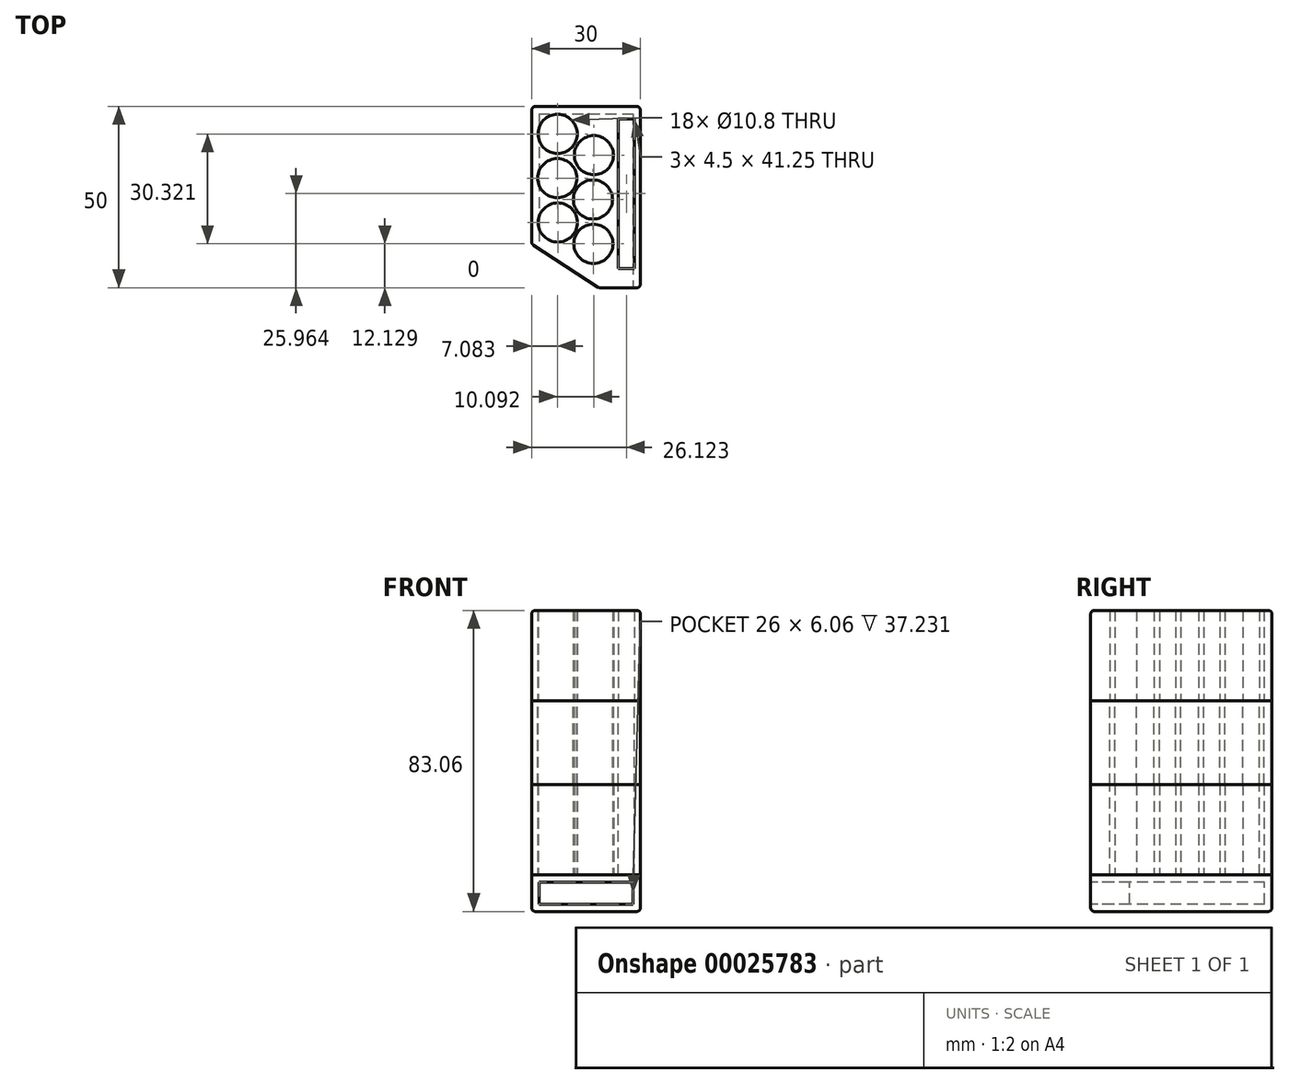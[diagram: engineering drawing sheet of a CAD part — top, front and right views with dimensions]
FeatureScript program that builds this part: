
annotation { "Feature Type Name" : "Feature", "Feature Type Description" : "" }
export const myFeature = defineFeature(function(context is Context, id is Id, definition is map)
    precondition{}
    {
        {
            var Q0;
            Q0=qCreatedBy(makeId("Top.planeOp"),FACE);
            var sketch = newSketch(context, id + "F0", { "sketchPlane" : qUnion([Q0])});
            skLineSegment(sketch, "E0.bottom", {"start": v(-10.19, 25.73) * mm, "end": v(19.81, 25.73) * mm});
            skLineSegment(sketch, "E0.top", {"start": v(8.4, -24.27) * mm, "end": v(19.81, -24.27) * mm});
            skLineSegment(sketch, "E0.left", {"start": v(-10.19, 25.73) * mm, "end": v(-10.19, -12.2) * mm});
            skLineSegment(sketch, "E0.right", {"start": v(19.81, 25.73) * mm, "end": v(19.81, -24.27) * mm});
            skCircle(sketch, "E1", {"center": v(-3.04, 18.18) * mm, "radius": 5.4 * mm});
            skCircle(sketch, "E2", {"center": v(6.98, 12.3) * mm, "radius": 5.4 * mm});
            skCircle(sketch, "E3", {"center": v(-3.1, 5.96) * mm, "radius": 5.4 * mm});
            skCircle(sketch, "E4", {"center": v(6.72, 0.09) * mm, "radius": 5.4 * mm});
            skCircle(sketch, "E5", {"center": v(-2.98, -6.26) * mm, "radius": 5.4 * mm});
            skCircle(sketch, "E6", {"center": v(6.85, -12.14) * mm, "radius": 5.4 * mm});
            skLineSegment(sketch, "E7.bottom", {"start": v(13.68, -18.93) * mm, "end": v(18.18, -18.93) * mm});
            skLineSegment(sketch, "E7.top", {"start": v(13.68, 22.32) * mm, "end": v(18.18, 22.32) * mm});
            skLineSegment(sketch, "E7.left", {"start": v(13.68, -18.93) * mm, "end": v(13.68, 22.32) * mm});
            skLineSegment(sketch, "E7.right", {"start": v(18.18, -18.93) * mm, "end": v(18.18, 22.32) * mm});
            skLineSegment(sketch, "E8", {"start": v(-10.19, -12.2) * mm, "end": v(8.4, -24.27) * mm});
            skSolve(sketch);
        }
        {
            var Q0;
            Q0=makeQuery(id+"F0.imprint","IMPRINT",FACE,{"disambiguationData":[TD([[makeQuery(id+"F0.imprint","IMPRINT",EDGE,{"derivedFrom":sQuery(id+"F0.wireOp",EDGE,"E0.bottom")}),-1.0]])]});
            extrude(context, id + "F1", {"entities" : qUnion([Q0]), "depth" : 25 * mm});
        }
        {
            var Q0;
            Q0=makeQuery(id+"F0.imprint","IMPRINT",FACE,{"disambiguationData":[TD([[makeQuery(id+"F0.imprint","IMPRINT",EDGE,{"derivedFrom":sQuery(id+"F0.wireOp",EDGE,"E7.bottom")}),1.0]])]});
            var Q1;
            Q1=makeQuery(id+"F0.imprint","IMPRINT",FACE,{"disambiguationData":[TD([[makeQuery(id+"F0.imprint","IMPRINT",EDGE,{"derivedFrom":sQuery(id+"F0.wireOp",EDGE,"E6")}),1.0]])]});
            var Q2;
            Q2=makeQuery(id+"F0.imprint","IMPRINT",FACE,{"disambiguationData":[TD([[makeQuery(id+"F0.imprint","IMPRINT",EDGE,{"derivedFrom":sQuery(id+"F0.wireOp",EDGE,"E5")}),1.0]])]});
            var Q3;
            Q3=makeQuery(id+"F0.imprint","IMPRINT",FACE,{"disambiguationData":[TD([[makeQuery(id+"F0.imprint","IMPRINT",EDGE,{"derivedFrom":sQuery(id+"F0.wireOp",EDGE,"E3")}),1.0]])]});
            var Q4;
            Q4=makeQuery(id+"F0.imprint","IMPRINT",FACE,{"disambiguationData":[TD([[makeQuery(id+"F0.imprint","IMPRINT",EDGE,{"derivedFrom":sQuery(id+"F0.wireOp",EDGE,"E4")}),1.0]])]});
            var Q5;
            Q5=makeQuery(id+"F0.imprint","IMPRINT",FACE,{"disambiguationData":[TD([[makeQuery(id+"F0.imprint","IMPRINT",EDGE,{"derivedFrom":sQuery(id+"F0.wireOp",EDGE,"E2")}),1.0]])]});
            var Q6;
            Q6=makeQuery(id+"F0.imprint","IMPRINT",FACE,{"disambiguationData":[TD([[makeQuery(id+"F0.imprint","IMPRINT",EDGE,{"derivedFrom":sQuery(id+"F0.wireOp",EDGE,"E1")}),1.0]])]});
            var Q7;
            Q7=makeQuery(id+"F0.imprint","IMPRINT",FACE,{"disambiguationData":[TD([[makeQuery(id+"F0.imprint","IMPRINT",EDGE,{"derivedFrom":sQuery(id+"F0.wireOp",EDGE,"E0.bottom")}),-1.0]])]});
            extrude(context, id + "F2", {"entities" : qUnion([Q0, Q1, Q2, Q3, Q4, Q5, Q6, Q7]), "oppositeDirection" : true, "depth" : 10.06 * mm});
        }
        {
            var Q0;
            Q0=makeQuery(id+"F1.opExtrude","CAP_FACE",FACE,{"disambiguationData":[OSD([sQuery(id+"F0.wireOp",EDGE,"E0.bottom"),sQuery(id+"F0.wireOp",EDGE,"E0.top"),sQuery(id+"F0.wireOp",EDGE,"E0.left"),sQuery(id+"F0.wireOp",EDGE,"E0.right"),sQuery(id+"F0.wireOp",EDGE,"E1"),sQuery(id+"F0.wireOp",EDGE,"E2"),sQuery(id+"F0.wireOp",EDGE,"E3"),sQuery(id+"F0.wireOp",EDGE,"E4"),sQuery(id+"F0.wireOp",EDGE,"E5"),sQuery(id+"F0.wireOp",EDGE,"E6"),sQuery(id+"F0.wireOp",EDGE,"E7.bottom"),sQuery(id+"F0.wireOp",EDGE,"E7.top"),sQuery(id+"F0.wireOp",EDGE,"E7.left"),sQuery(id+"F0.wireOp",EDGE,"E7.right"),sQuery(id+"F0.wireOp",EDGE,"E8")])],"isStart":false});
            var sketch = newSketch(context, id + "F3", { "sketchPlane" : qUnion([Q0])});
            skLineSegment(sketch, "E9.bottom", {"start": v(13.68, -18.93) * mm, "end": v(18.18, -18.93) * mm});
            skLineSegment(sketch, "E9.top", {"start": v(13.68, 22.32) * mm, "end": v(18.18, 22.32) * mm});
            skLineSegment(sketch, "E9.left", {"start": v(13.68, -18.93) * mm, "end": v(13.68, 22.32) * mm});
            skLineSegment(sketch, "E9.right", {"start": v(18.18, -18.93) * mm, "end": v(18.18, 22.32) * mm});
            skSolve(sketch);
        }
        {
            var Q0;
            Q0 = qSketchRegion(id + "F3", true);
            extrude(context, id + "F4", {"entities" : qUnion([Q0]), "oppositeDirection" : true, "depth" : 25 * mm});
        }
        {
            var Q0;
            Q0=makeQuery(id+"F1.opExtrude","SWEPT_BODY",BODY,{"disambiguationData":[OSD([sQuery(id+"F0.wireOp",EDGE,"E0.bottom"),sQuery(id+"F0.wireOp",EDGE,"E0.top"),sQuery(id+"F0.wireOp",EDGE,"E0.left"),sQuery(id+"F0.wireOp",EDGE,"E0.right"),sQuery(id+"F0.wireOp",EDGE,"E1"),sQuery(id+"F0.wireOp",EDGE,"E2"),sQuery(id+"F0.wireOp",EDGE,"E3"),sQuery(id+"F0.wireOp",EDGE,"E4"),sQuery(id+"F0.wireOp",EDGE,"E5"),sQuery(id+"F0.wireOp",EDGE,"E6"),sQuery(id+"F0.wireOp",EDGE,"E7.bottom"),sQuery(id+"F0.wireOp",EDGE,"E7.top"),sQuery(id+"F0.wireOp",EDGE,"E7.left"),sQuery(id+"F0.wireOp",EDGE,"E7.right"),sQuery(id+"F0.wireOp",EDGE,"E8")])]});
            var Q1;
            Q1=makeQuery(id+"F1.opExtrude","SWEPT_EDGE",EDGE,{"disambiguationData":[OSD([sQuery(id+"F0.wireOp",EDGE,"E0.top"),sQuery(id+"F0.wireOp",EDGE,"E0.right")])]});
            var Q2;
            Q2=makeQuery(id+"F1.opExtrude","CAP_VERTEX",VERTEX,{"disambiguationData":[OSD([sQuery(id+"F0.wireOp",EDGE,"E0.top"),sQuery(id+"F0.wireOp",EDGE,"E0.right")])],"isStart":false});
            transform(context, id + "F5", {"entities" : qUnion([Q0]), "transformType" : TransformType.TRANSLATION_DISTANCE, "transformDirection" : qUnion([Q1]), "distance" : 48 * mm, "oppositeDirection" : true, "makeCopy" : true});
        }
        {
            var Q0;
            Q0=makeQuery(id+"F2.opExtrude","SWEPT_FACE",FACE,{"disambiguationData":[OSD([sQuery(id+"F0.wireOp",EDGE,"E0.top")])]});
            var Q1;
            Q1=makeQuery(id+"F2.opExtrude","SWEPT_FACE",FACE,{"disambiguationData":[OSD([sQuery(id+"F0.wireOp",EDGE,"E8")])]});
            shell(context, id + "F6", {"entities" : qUnion([Q0, Q1]), "thickness" : 2 * mm});
        }
        {
            var Q0;
            Q0=makeQuery(id+"F5.opPattern","COPY",EDGE,{"derivedFrom":makeQuery(id+"F1.opExtrude","CAP_EDGE",EDGE,{"disambiguationData":[OSD([sQuery(id+"F0.wireOp",EDGE,"E0.left")])],"isStart":false}),"instanceName":"1"});
            var Q1;
            Q1=makeQuery(id+"F5.opPattern","COPY",EDGE,{"derivedFrom":makeQuery(id+"F1.opExtrude","CAP_EDGE",EDGE,{"disambiguationData":[OSD([sQuery(id+"F0.wireOp",EDGE,"E8")])],"isStart":false}),"instanceName":"1"});
            var Q2;
            Q2=makeQuery(id+"F5.opPattern","COPY",EDGE,{"derivedFrom":makeQuery(id+"F1.opExtrude","CAP_EDGE",EDGE,{"disambiguationData":[OSD([sQuery(id+"F0.wireOp",EDGE,"E0.top")])],"isStart":false}),"instanceName":"1"});
            var Q3;
            Q3=makeQuery(id+"F5.opPattern","COPY",EDGE,{"derivedFrom":makeQuery(id+"F1.opExtrude","CAP_EDGE",EDGE,{"disambiguationData":[OSD([sQuery(id+"F0.wireOp",EDGE,"E0.bottom")])],"isStart":false}),"instanceName":"1"});
            var Q4;
            Q4=makeQuery(id+"F5.opPattern","COPY",EDGE,{"derivedFrom":makeQuery(id+"F1.opExtrude","CAP_EDGE",EDGE,{"disambiguationData":[OSD([sQuery(id+"F0.wireOp",EDGE,"E0.right")])],"isStart":false}),"instanceName":"1"});
            fillet(context, id + "F7", {"entities" : qUnion([Q0, Q1, Q2, Q3, Q4]), "radius" : 1 * mm, "tangentPropagation" : true, "allowEdgeOverflow" : false});
        }
        {
            var Q0;
            Q0=makeQuery(id+"F2.opExtrude","CAP_EDGE",EDGE,{"disambiguationData":[OSD([sQuery(id+"F0.wireOp",EDGE,"E0.left")])],"isStart":false});
            var Q1;
            Q1=makeQuery(id+"F2.opExtrude","CAP_EDGE",EDGE,{"disambiguationData":[OSD([sQuery(id+"F0.wireOp",EDGE,"E8")])],"isStart":false});
            var Q2;
            Q2=makeQuery(id+"F2.opExtrude","CAP_EDGE",EDGE,{"disambiguationData":[OSD([sQuery(id+"F0.wireOp",EDGE,"E0.top")])],"isStart":false});
            var Q3;
            Q3=makeQuery(id+"F2.opExtrude","CAP_EDGE",EDGE,{"disambiguationData":[OSD([sQuery(id+"F0.wireOp",EDGE,"E0.right")])],"isStart":false});
            var Q4;
            Q4=makeQuery(id+"F2.opExtrude","CAP_EDGE",EDGE,{"disambiguationData":[OSD([sQuery(id+"F0.wireOp",EDGE,"E0.bottom")])],"isStart":false});
            fillet(context, id + "F8", {"entities" : qUnion([Q0, Q1, Q2, Q3, Q4]), "radius" : 1 * mm, "tangentPropagation" : true, "allowEdgeOverflow" : false});
        }
        {
            var Q0;
            Q0=makeQuery(id+"F5.opPattern","COPY",FACE,{"derivedFrom":makeQuery(id+"F1.opExtrude","CAP_FACE",FACE,{"disambiguationData":[OSD([sQuery(id+"F0.wireOp",EDGE,"E0.bottom"),sQuery(id+"F0.wireOp",EDGE,"E0.top"),sQuery(id+"F0.wireOp",EDGE,"E0.left"),sQuery(id+"F0.wireOp",EDGE,"E0.right"),sQuery(id+"F0.wireOp",EDGE,"E1"),sQuery(id+"F0.wireOp",EDGE,"E2"),sQuery(id+"F0.wireOp",EDGE,"E3"),sQuery(id+"F0.wireOp",EDGE,"E4"),sQuery(id+"F0.wireOp",EDGE,"E5"),sQuery(id+"F0.wireOp",EDGE,"E6"),sQuery(id+"F0.wireOp",EDGE,"E7.bottom"),sQuery(id+"F0.wireOp",EDGE,"E7.top"),sQuery(id+"F0.wireOp",EDGE,"E7.left"),sQuery(id+"F0.wireOp",EDGE,"E7.right"),sQuery(id+"F0.wireOp",EDGE,"E8")])],"isStart":true}),"instanceName":"1"});
            extrude(context, id + "F9", {"entities" : qUnion([Q0]), "depth" : 23 * mm});
        }
        {
            var Q0;
            Q0=makeQuery(id+"F5.opPattern","COPY",EDGE,{"derivedFrom":makeQuery(id+"F1.opExtrude","SWEPT_EDGE",EDGE,{"disambiguationData":[OSD([sQuery(id+"F0.wireOp",EDGE,"E0.left"),sQuery(id+"F0.wireOp",EDGE,"E8")])]}),"instanceName":"1"});
            var Q1;
            Q1=makeQuery(id+"F9.opExtrude","SWEPT_EDGE",EDGE,{"disambiguationData":[OSD([sQuery(id+"F0.wireOp",EDGE,"E0.left"),sQuery(id+"F0.wireOp",EDGE,"E8")])]});
            var Q2;
            Q2=makeQuery(id+"F1.opExtrude","SWEPT_EDGE",EDGE,{"disambiguationData":[OSD([sQuery(id+"F0.wireOp",EDGE,"E0.left"),sQuery(id+"F0.wireOp",EDGE,"E8")])]});
            var Q3;
            Q3=makeQuery(id+"F5.opPattern","COPY",EDGE,{"derivedFrom":makeQuery(id+"F1.opExtrude","SWEPT_EDGE",EDGE,{"disambiguationData":[OSD([sQuery(id+"F0.wireOp",EDGE,"E0.top"),sQuery(id+"F0.wireOp",EDGE,"E8")])]}),"instanceName":"1"});
            var Q4;
            Q4=makeQuery(id+"F9.opExtrude","SWEPT_EDGE",EDGE,{"disambiguationData":[OSD([sQuery(id+"F0.wireOp",EDGE,"E0.top"),sQuery(id+"F0.wireOp",EDGE,"E8")])]});
            var Q5;
            Q5=makeQuery(id+"F1.opExtrude","SWEPT_EDGE",EDGE,{"disambiguationData":[OSD([sQuery(id+"F0.wireOp",EDGE,"E0.top"),sQuery(id+"F0.wireOp",EDGE,"E8")])]});
            var Q6;
            Q6=makeQuery(id+"F5.opPattern","COPY",EDGE,{"derivedFrom":makeQuery(id+"F1.opExtrude","SWEPT_EDGE",EDGE,{"disambiguationData":[OSD([sQuery(id+"F0.wireOp",EDGE,"E0.top"),sQuery(id+"F0.wireOp",EDGE,"E0.right")])]}),"instanceName":"1"});
            var Q7;
            Q7=makeQuery(id+"F9.opExtrude","SWEPT_EDGE",EDGE,{"disambiguationData":[OSD([sQuery(id+"F0.wireOp",EDGE,"E0.top"),sQuery(id+"F0.wireOp",EDGE,"E0.right")])]});
            var Q8;
            Q8=makeQuery(id+"F1.opExtrude","SWEPT_EDGE",EDGE,{"disambiguationData":[OSD([sQuery(id+"F0.wireOp",EDGE,"E0.top"),sQuery(id+"F0.wireOp",EDGE,"E0.right")])]});
            var Q9;
            Q9=makeQuery(id+"F5.opPattern","COPY",EDGE,{"derivedFrom":makeQuery(id+"F1.opExtrude","SWEPT_EDGE",EDGE,{"disambiguationData":[OSD([sQuery(id+"F0.wireOp",EDGE,"E0.bottom"),sQuery(id+"F0.wireOp",EDGE,"E0.right")])]}),"instanceName":"1"});
            var Q10;
            Q10=makeQuery(id+"F9.opExtrude","SWEPT_EDGE",EDGE,{"disambiguationData":[OSD([sQuery(id+"F0.wireOp",EDGE,"E0.bottom"),sQuery(id+"F0.wireOp",EDGE,"E0.right")])]});
            var Q11;
            Q11=makeQuery(id+"F1.opExtrude","SWEPT_EDGE",EDGE,{"disambiguationData":[OSD([sQuery(id+"F0.wireOp",EDGE,"E0.bottom"),sQuery(id+"F0.wireOp",EDGE,"E0.right")])]});
            var Q12;
            Q12=makeQuery(id+"F1.opExtrude","SWEPT_EDGE",EDGE,{"disambiguationData":[OSD([sQuery(id+"F0.wireOp",EDGE,"E0.bottom"),sQuery(id+"F0.wireOp",EDGE,"E0.left")])]});
            var Q13;
            Q13=makeQuery(id+"F9.opExtrude","SWEPT_EDGE",EDGE,{"disambiguationData":[OSD([sQuery(id+"F0.wireOp",EDGE,"E0.bottom"),sQuery(id+"F0.wireOp",EDGE,"E0.left")])]});
            var Q14;
            Q14=makeQuery(id+"F5.opPattern","COPY",EDGE,{"derivedFrom":makeQuery(id+"F1.opExtrude","SWEPT_EDGE",EDGE,{"disambiguationData":[OSD([sQuery(id+"F0.wireOp",EDGE,"E0.bottom"),sQuery(id+"F0.wireOp",EDGE,"E0.left")])]}),"instanceName":"1"});
            var Q15;
            Q15=makeQuery(id+"F2.opExtrude","SWEPT_EDGE",EDGE,{"disambiguationData":[OSD([sQuery(id+"F0.wireOp",EDGE,"E0.bottom"),sQuery(id+"F0.wireOp",EDGE,"E0.left")])]});
            var Q16;
            Q16=makeQuery(id+"F2.opExtrude","SWEPT_EDGE",EDGE,{"disambiguationData":[OSD([sQuery(id+"F0.wireOp",EDGE,"E0.left"),sQuery(id+"F0.wireOp",EDGE,"E8")])]});
            var Q17;
            Q17=makeQuery(id+"F6.opShell","OFFSET_EDGE",EDGE,{"disambiguationData":[OSD([sQuery(id+"F0.wireOp",EDGE,"E0.top"),sQuery(id+"F0.wireOp",EDGE,"E8")])]});
            var Q18;
            Q18=makeQuery(id+"F2.opExtrude","SWEPT_EDGE",EDGE,{"disambiguationData":[OSD([sQuery(id+"F0.wireOp",EDGE,"E0.top"),sQuery(id+"F0.wireOp",EDGE,"E8")])]});
            var Q19;
            Q19=makeQuery(id+"F2.opExtrude","SWEPT_EDGE",EDGE,{"disambiguationData":[OSD([sQuery(id+"F0.wireOp",EDGE,"E0.top"),sQuery(id+"F0.wireOp",EDGE,"E0.right")])]});
            var Q20;
            Q20=makeQuery(id+"F2.opExtrude","SWEPT_EDGE",EDGE,{"disambiguationData":[OSD([sQuery(id+"F0.wireOp",EDGE,"E0.bottom"),sQuery(id+"F0.wireOp",EDGE,"E0.right")])]});
            fillet(context, id + "F10", {"entities" : qUnion([Q0, Q1, Q2, Q3, Q4, Q5, Q6, Q7, Q8, Q9, Q10, Q11, Q12, Q13, Q14, Q15, Q16, Q17, Q18, Q19, Q20]), "radius" : 1 * mm, "tangentPropagation" : true, "allowEdgeOverflow" : false});
        }
    });
